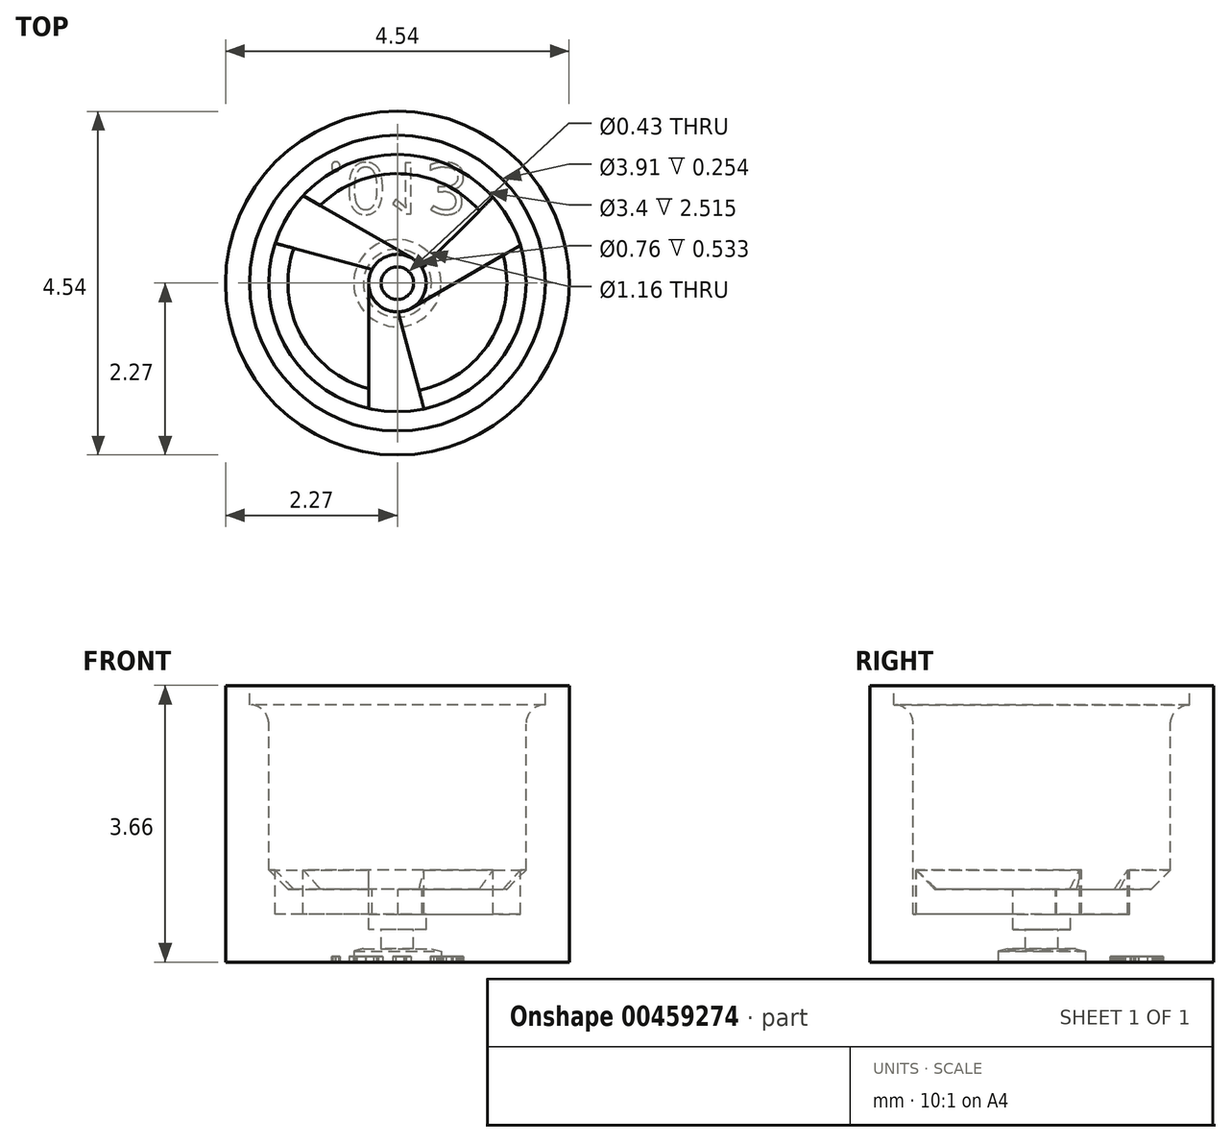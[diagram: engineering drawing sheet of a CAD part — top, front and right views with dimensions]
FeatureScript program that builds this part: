
annotation { "Feature Type Name" : "Feature", "Feature Type Description" : "" }
export const myFeature = defineFeature(function(context is Context, id is Id, definition is map)
    precondition{}
    {
        {
            var Q0;
            Q0=qCreatedBy(makeId("Top.planeOp"),FACE);
            var sketch = newSketch(context, id + "F0", { "sketchPlane" : qUnion([Q0])});
            skCircle(sketch, "E0", {"center": v(0, 0) * mm, "radius": 2.27 * mm});
            skSolve(sketch);
        }
        {
            var Q0;
            Q0 = qSketchRegion(id + "F0", true);
            extrude(context, id + "F1", {"entities" : qUnion([Q0]), "depth" : 3.66 * mm});
        }
        {
            var Q0;
            Q0=makeQuery(id+"F1.opExtrude","CAP_FACE",FACE,{"disambiguationData":[OSD([sQuery(id+"F0.wireOp",EDGE,"E0")])],"isStart":false});
            var sketch = newSketch(context, id + "F2", { "sketchPlane" : qUnion([Q0])});
            skCircle(sketch, "E1", {"center": v(0, 0) * mm, "radius": 1.96 * mm});
            skSolve(sketch);
        }
        {
            var Q0;
            Q0=makeQuery(id+"F2.imprint","IMPRINT",FACE,{"disambiguationData":[TD([[makeQuery(id+"F2.imprint","IMPRINT",EDGE,{"derivedFrom":sQuery(id+"F2.wireOp",EDGE,"E1")}),1.0]])]});
            extrude(context, id + "F3", {"entities" : qUnion([Q0]), "operationType" : NewBodyOperationType.REMOVE, "oppositeDirection" : true, "depth" : 0.25 * mm});
        }
        {
            var Q0;
            Q0=makeQuery(id+"F3.boolean.opBoolean","COPY",FACE,{"derivedFrom":makeQuery(id+"F3.opExtrude","CAP_FACE",FACE,{"disambiguationData":[OSD([sQuery(id+"F2.wireOp",EDGE,"E1")])],"isStart":false})});
            var sketch = newSketch(context, id + "F4", { "sketchPlane" : qUnion([Q0])});
            skCircle(sketch, "E2", {"center": v(0, 0) * mm, "radius": 1.7 * mm});
            skSolve(sketch);
        }
        {
            var Q0;
            Q0=makeQuery(id+"F4.imprint","IMPRINT",FACE,{"disambiguationData":[TD([[makeQuery(id+"F4.imprint","IMPRINT",EDGE,{"derivedFrom":sQuery(id+"F4.wireOp",EDGE,"E2")}),1.0]])]});
            extrude(context, id + "F5", {"entities" : qUnion([Q0]), "operationType" : NewBodyOperationType.REMOVE, "oppositeDirection" : true, "depth" : 2.44 * mm});
        }
        {
            var Q0;
            Q0=makeQuery(id+"F5.boolean.opBoolean","COPY",EDGE,{"derivedFrom":makeQuery(id+"F5.opExtrude","CAP_EDGE",EDGE,{"disambiguationData":[OSD([sQuery(id+"F4.wireOp",EDGE,"E2")])],"isStart":false})});
            chamfer(context, id + "F6", {"entities" : qUnion([Q0]), "chamferType" : ChamferType.OFFSET_ANGLE, "width" : 0.25 * mm, "oppositeDirection" : false, "angle" : 45 * degree, "tangentPropagation" : true});
        }
        {
            var Q0;
            Q0=makeQuery(id+"F5.boolean.opBoolean","COPY",FACE,{"derivedFrom":makeQuery(id+"F5.opExtrude","CAP_FACE",FACE,{"disambiguationData":[OSD([sQuery(id+"F4.wireOp",EDGE,"E2")])],"isStart":false})});
            var sketch = newSketch(context, id + "F7", { "sketchPlane" : qUnion([Q0])});
            skCircle(sketch, "E3", {"center": v(0, 0) * mm, "radius": 0.38 * mm});
            skSolve(sketch);
        }
        {
            var Q0;
            Q0=makeQuery(id+"F7.imprint","IMPRINT",FACE,{"disambiguationData":[TD([[makeQuery(id+"F7.imprint","IMPRINT",EDGE,{"derivedFrom":sQuery(id+"F7.wireOp",EDGE,"E3")}),1.0]])]});
            extrude(context, id + "F8", {"entities" : qUnion([Q0]), "operationType" : NewBodyOperationType.REMOVE, "oppositeDirection" : true, "depth" : 0.53 * mm});
        }
        {
            var Q0;
            Q0=makeQuery(id+"F8.boolean.opBoolean","COPY",FACE,{"derivedFrom":makeQuery(id+"F8.opExtrude","CAP_FACE",FACE,{"disambiguationData":[OSD([sQuery(id+"F7.wireOp",EDGE,"E3")])],"isStart":false})});
            var sketch = newSketch(context, id + "F9", { "sketchPlane" : qUnion([Q0])});
            skCircle(sketch, "E4", {"center": v(0, 0) * mm, "radius": 0.21 * mm});
            skSolve(sketch);
        }
        {
            var Q0;
            Q0=makeQuery(id+"F9.imprint","IMPRINT",FACE,{"disambiguationData":[TD([[makeQuery(id+"F9.imprint","IMPRINT",EDGE,{"derivedFrom":sQuery(id+"F9.wireOp",EDGE,"E4")}),1.0]])]});
            extrude(context, id + "F10", {"entities" : qUnion([Q0]), "operationType" : NewBodyOperationType.REMOVE, "oppositeDirection" : true, "depth" : 25.4 * mm});
        }
        {
            var Q0;
            Q0=makeQuery(id+"F1.opExtrude","CAP_FACE",FACE,{"disambiguationData":[OSD([sQuery(id+"F0.wireOp",EDGE,"E0")])],"isStart":true});
            var sketch = newSketch(context, id + "F11", { "sketchPlane" : qUnion([Q0])});
            skCircle(sketch, "E5", {"center": v(0, 0) * mm, "radius": 0.58 * mm});
            skSolve(sketch);
        }
        {
            var Q0;
            Q0=makeQuery(id+"F11.imprint","IMPRINT",FACE,{"disambiguationData":[TD([[makeQuery(id+"F11.imprint","IMPRINT",EDGE,{"derivedFrom":sQuery(id+"F11.wireOp",EDGE,"E5")}),1.0]])]});
            extrude(context, id + "F12", {"entities" : qUnion([Q0]), "operationType" : NewBodyOperationType.REMOVE, "oppositeDirection" : true, "depth" : 0.18 * mm});
        }
        {
            var Q0;
            Q0=makeQuery(id+"F12.boolean.opBoolean","COPY",EDGE,{"derivedFrom":makeQuery(id+"F12.opExtrude","CAP_EDGE",EDGE,{"disambiguationData":[OSD([sQuery(id+"F11.wireOp",EDGE,"E5")])],"isStart":false})});
            chamfer(context, id + "F13", {"entities" : qUnion([Q0]), "chamferType" : ChamferType.OFFSET_ANGLE, "width" : 0.13 * mm, "oppositeDirection" : false, "angle" : 15 * degree, "tangentPropagation" : true});
        }
        {
            var Q0;
            Q0=makeQuery(id+"F5.boolean.opBoolean","COPY",FACE,{"derivedFrom":makeQuery(id+"F5.opExtrude","CAP_FACE",FACE,{"disambiguationData":[OSD([sQuery(id+"F4.wireOp",EDGE,"E2")])],"isStart":false})});
            var sketch = newSketch(context, id + "F14", { "sketchPlane" : qUnion([Q0])});
            skArc(sketch, "E6.0", {"start": v(0.2, 0.33) * mm, "mid": v(-0.1, 0.37) * mm, "end": v(-0.33, 0.18) * mm});
            skArc(sketch, "E7.0", {"start": v(-1.25, 1.16) * mm, "mid": v(-1.47, 0.86) * mm, "end": v(-1.62, 0.53) * mm});
            skLineSegment(sketch, "E8", {"start": v(0.2, 0.33) * mm, "end": v(-1.25, 1.16) * mm});
            skLineSegment(sketch, "E9", {"start": v(-0.33, 0.18) * mm, "end": v(-1.62, 0.53) * mm});
            skLineSegment(sketch, "E10.1.0", {"start": v(-0.38, 0) * mm, "end": v(-0.38, -1.66) * mm});
            skArc(sketch, "E10.1.1", {"start": v(-0.38, 0) * mm, "mid": v(-0.27, -0.27) * mm, "end": v(0, -0.38) * mm});
            skLineSegment(sketch, "E10.1.2", {"start": v(0, -0.38) * mm, "end": v(0.35, -1.66) * mm});
            skArc(sketch, "E10.1.3", {"start": v(-0.38, -1.66) * mm, "mid": v(-0.01, -1.7) * mm, "end": v(0.35, -1.66) * mm});
            skLineSegment(sketch, "E10.2.0", {"start": v(0.2, -0.33) * mm, "end": v(1.63, 0.5) * mm});
            skArc(sketch, "E10.2.1", {"start": v(0.2, -0.33) * mm, "mid": v(0.37, -0.1) * mm, "end": v(0.33, 0.2) * mm});
            skLineSegment(sketch, "E10.2.2", {"start": v(0.33, 0.2) * mm, "end": v(1.27, 1.14) * mm});
            skArc(sketch, "E10.2.3", {"start": v(1.63, 0.5) * mm, "mid": v(1.48, 0.84) * mm, "end": v(1.27, 1.14) * mm});
            skSolve(sketch);
        }
        {
            var Q0;
            Q0 = qSketchRegion(id + "F14", true);
            extrude(context, id + "F15", {"entities" : qUnion([Q0]), "operationType" : NewBodyOperationType.REMOVE, "oppositeDirection" : true, "depth" : 0.33 * mm});
        }
        {
            var Q0;
            Q0 = qSketchRegion(id + "F14", true);
            extrude(context, id + "F16", {"entities" : qUnion([Q0]), "operationType" : NewBodyOperationType.REMOVE, "depth" : 25.4 * mm});
        }
        {
            var Q0;
            Q0=makeQuery(id+"F16.boolean.opBoolean","INTERSECT",EDGE,{"derivedFrom":[makeQuery(id+"F16.opExtrude","SWEPT_FACE",FACE,{"disambiguationData":[OSD([sQuery(id+"F14.wireOp",EDGE,"E7.0")])]}),makeQuery(id+"F16.opExtrude","SWEPT_FACE",FACE,{"disambiguationData":[OSD([sQuery(id+"F14.wireOp",EDGE,"E10.1.3")])]}),makeQuery(id+"F16.opExtrude","SWEPT_FACE",FACE,{"disambiguationData":[OSD([sQuery(id+"F14.wireOp",EDGE,"E10.2.3")])]})]});
            fillet(context, id + "F17", {"entities" : qUnion([Q0]), "radius" : 0.25 * mm, "tangentPropagation" : true, "allowEdgeOverflow" : false});
        }
        {
            var Q0;
            Q0=makeQuery(id+"F1.opExtrude","CAP_FACE",FACE,{"disambiguationData":[OSD([sQuery(id+"F0.wireOp",EDGE,"E0")])],"isStart":true});
            var sketch = newSketch(context, id + "F18", { "sketchPlane" : qUnion([Q0])});
            skText(sketch, "E11", { "text": ".013", "fontName": "OpenSans-Regular.ttf"});
            const initialGuessF18  = {"E11": [-0.00094, -0.00159, 1, 0, 0.00068]};
            skSetInitialGuess(sketch, initialGuessF18);
            skSolve(sketch);
        }
        {
            var Q0;
            Q0 = qSketchRegion(id + "F18", true);
            extrude(context, id + "F19", {"entities" : qUnion([Q0]), "operationType" : NewBodyOperationType.REMOVE, "oppositeDirection" : true, "depth" : 0.08 * mm});
        }
    });
